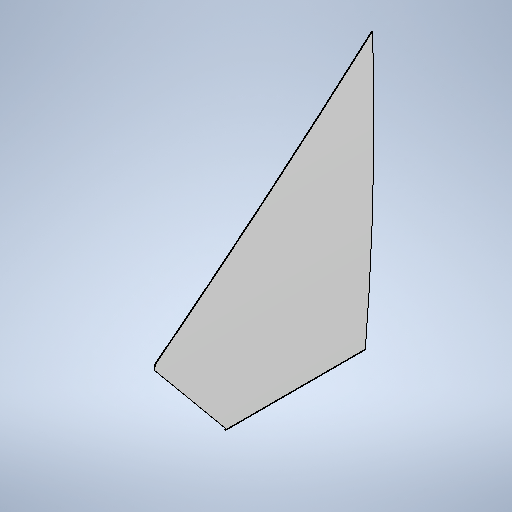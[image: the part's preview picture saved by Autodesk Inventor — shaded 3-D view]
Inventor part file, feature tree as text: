
AUTODESK INVENTOR PART (.ipt)
format: ipt  version: 2025 (Build 290162010, 162A)  size: 486,400 bytes
history: native  units: mm
features: other x4, sheet_metal_op x3, sketch x3, projected_geometry x2, extrude x1
ambient origin geometry x8: Origin, YZ Plane, XZ Plane, XY Plane, X Axis, Y Axis, Z Axis, Center Point
bodies: Body1 (feature_tree)
feature tree (13):
  sheet_metal_op  "Contour Flange2"
  extrude  "Extrusion2"  Depth=3.0mm
  other  "Mark4"
  other  "A-Side Definition"
  sketch  "Sketch1"  dims[d36=3.0mm d37=3.0mm]
  other  "Plate2"
  sheet_metal_op  "Bend2"
  sheet_metal_op  "Corner2"
  sketch  "Sketch2"  dims[d38=1.5mm]
  projected_geometry  "Projected Loop5"
  projected_geometry  "Projected Loop6"
  sketch  "Sketch6"  dims[d39=6.0mm d40=5.0mm d41=980.0mm d42=5.0mm d43=3.0mm d44=12.0mm d45=3.0mm d46=5.0mm d65=8.0mm d78=3.0mm d80=3.0mm d123=0.0mm d124=0.0mm d153=5.0mm d154=63.0mm d155=11050.0mm d156=23.736478mm d158=5.0mm d160=300.0mm d162=6.981317mm d163=6.981317mm d172=578.0mm d174=1843.0mm d175=0.0mm d176=1.0mm]
  other  "Definition1"
